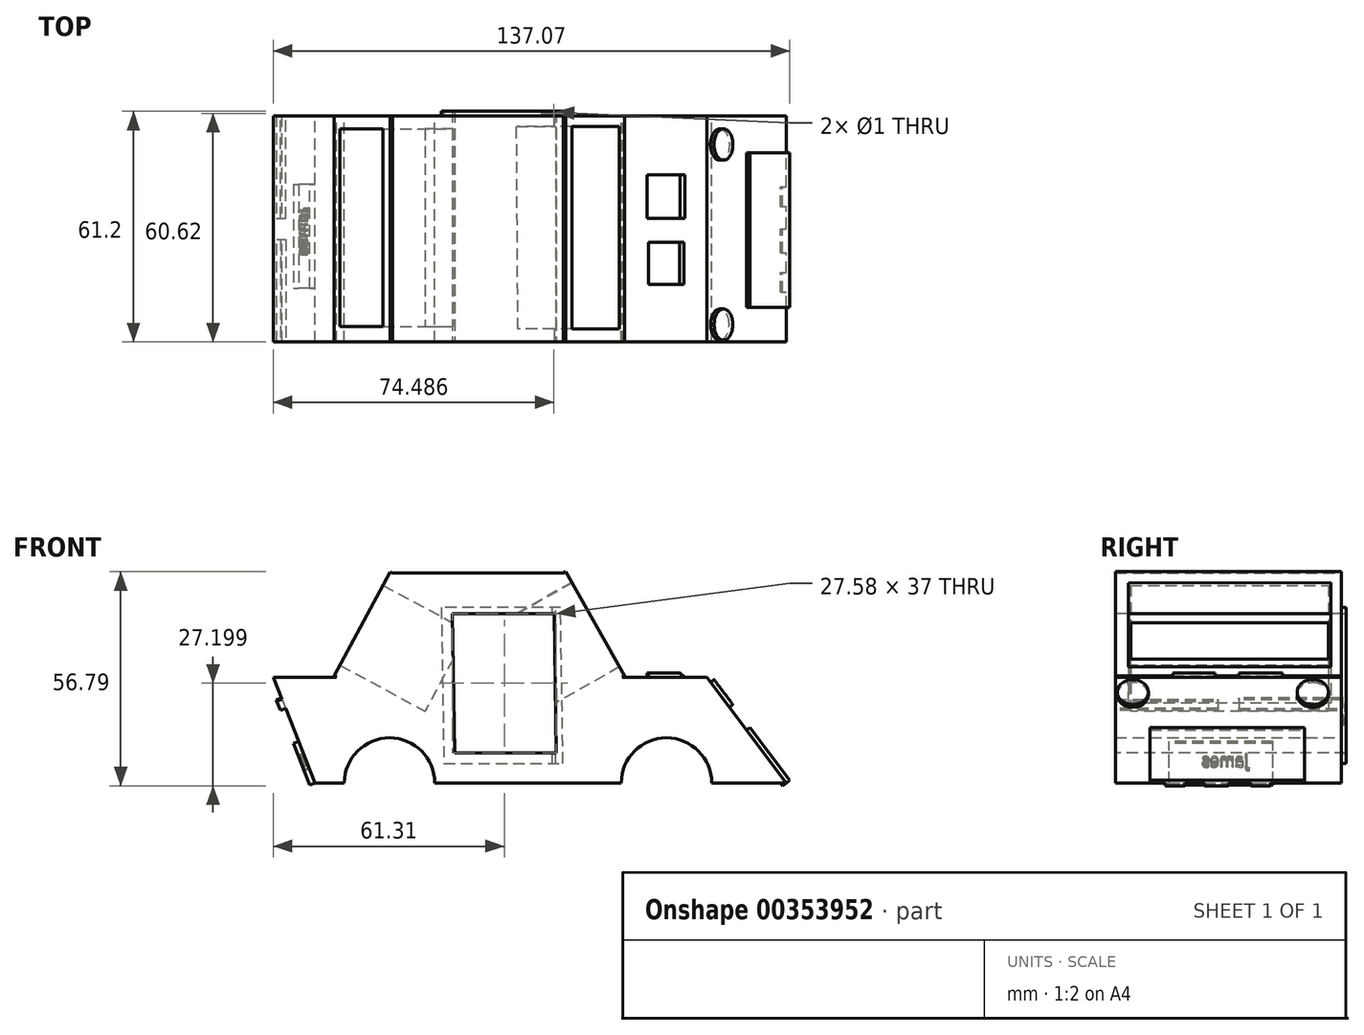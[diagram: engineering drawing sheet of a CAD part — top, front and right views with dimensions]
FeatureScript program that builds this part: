
annotation { "Feature Type Name" : "Feature", "Feature Type Description" : "" }
export const myFeature = defineFeature(function(context is Context, id is Id, definition is map)
    precondition{}
    {
        {
            var Q0;
            Q0=qCreatedBy(makeId("Front.planeOp"),FACE);
            var sketch = newSketch(context, id + "F0", { "sketchPlane" : qUnion([Q0])});
            skLineSegment(sketch, "E0", {"start": v(-59.7, -21.02) * mm, "end": v(-51.97, -21.02) * mm});
            skLineSegment(sketch, "E1", {"start": v(65.31, -21.02) * mm, "end": v(44.23, 7.04) * mm});
            skLineSegment(sketch, "E2", {"start": v(44.23, 7.04) * mm, "end": v(-70.8, 7.04) * mm});
            skLineSegment(sketch, "E3", {"start": v(-70.8, 7.04) * mm, "end": v(-59.7, -21.02) * mm});
            skLineSegment(sketch, "E4", {"start": v(-54.05, 7.04) * mm, "end": v(-39.17, 34.7) * mm});
            skLineSegment(sketch, "E5", {"start": v(-39.17, 34.7) * mm, "end": v(6.2, 34.7) * mm});
            skLineSegment(sketch, "E6", {"start": v(6.2, 34.7) * mm, "end": v(21.82, 7.04) * mm});
            skArc(sketch, "E7", {"start": v(-27.97, -21.02) * mm, "mid": v(-39.97, -9.02) * mm, "end": v(-51.97, -21.02) * mm});
            skArc(sketch, "E8", {"start": v(45.54, -21.02) * mm, "mid": v(33.54, -9.02) * mm, "end": v(21.54, -21.02) * mm});
            skLineSegment(sketch, "E9.trimOffspring", {"start": v(-27.97, -21.02) * mm, "end": v(21.54, -21.02) * mm});
            skLineSegment(sketch, "E10.trimOffspring", {"start": v(45.54, -21.02) * mm, "end": v(65.31, -21.02) * mm});
            skSolve(sketch);
        }
        {
            var Q0;
            {var subQ0=sQuery(id+"F0.wireOp",EDGE,"E4");Q0=makeQuery(id+"F0.imprint","IMPRINT",FACE,{"disambiguationData":[TD([[makeQuery(id+"F0.imprint","IMPRINT",EDGE,{"derivedFrom":subQ0}),-1.0]])]});}
            var Q1;
            Q1=makeQuery(id+"F0.imprint","IMPRINT",FACE,{"disambiguationData":[TD([[makeQuery(id+"F0.imprint","IMPRINT",EDGE,{"derivedFrom":sQuery(id+"F0.wireOp",EDGE,"E0")}),1.0]])]});
            extrude(context, id + "F1", {"entities" : qUnion([Q0, Q1]), "endBound" : BoundingType.SYMMETRIC, "depth" : 60 * mm});
        }
        {
            var Q0;
            Q0=makeQuery(id+"F1.opExtrude","SWEPT_FACE",FACE,{"disambiguationData":[OSD([sQuery(id+"F0.wireOp",EDGE,"E1")])]});
            var sketch = newSketch(context, id + "F2", { "sketchPlane" : qUnion([Q0])});
            skCircle(sketch, "E11", {"center": v(-25.38, -26.75) * mm, "radius": 4.12 * mm});
            skCircle(sketch, "E12", {"center": v(22.39, -26.75) * mm, "radius": 4.16 * mm});
            skLineSegment(sketch, "E13", {"start": v(-20.79, -38.5) * mm, "end": v(-20.79, -56.04) * mm});
            skPoint(sketch, "E13.startSnap0", {"position": v(-30, -38.5) * mm});
            skLineSegment(sketch, "E14", {"start": v(-20.79, -38.5) * mm, "end": v(20.19, -38.5) * mm});
            skLineSegment(sketch, "E15", {"start": v(20.19, -38.5) * mm, "end": v(20.19, -56.04) * mm});
            skLineSegment(sketch, "E16", {"start": v(-16.59, -38.5) * mm, "end": v(-16.59, -56.04) * mm});
            skLineSegment(sketch, "E17", {"start": v(-16.59, -56.04) * mm, "end": v(-11.8, -56.04) * mm});
            skLineSegment(sketch, "E18", {"start": v(-11.8, -56.04) * mm, "end": v(-11.8, -38.5) * mm});
            skLineSegment(sketch, "E19", {"start": v(-11.8, -38.5) * mm, "end": v(-7.8, -38.5) * mm});
            skLineSegment(sketch, "E20", {"start": v(-7.8, -38.5) * mm, "end": v(-7.8, -56.04) * mm});
            skLineSegment(sketch, "E21", {"start": v(-7.8, -56.04) * mm, "end": v(-4.2, -56.04) * mm});
            skLineSegment(sketch, "E22", {"start": v(-4.2, -56.04) * mm, "end": v(-4.2, -38.5) * mm});
            skLineSegment(sketch, "E23", {"start": v(-4.2, -38.5) * mm, "end": v(0, -38.5) * mm});
            skLineSegment(sketch, "E24", {"start": v(0, -38.5) * mm, "end": v(0, -56.04) * mm});
            skLineSegment(sketch, "E25", {"start": v(0, -56.04) * mm, "end": v(4.2, -56.04) * mm});
            skLineSegment(sketch, "E26", {"start": v(4.2, -56.04) * mm, "end": v(4.2, -38.5) * mm});
            skLineSegment(sketch, "E27", {"start": v(4.2, -38.5) * mm, "end": v(8.6, -38.5) * mm});
            skLineSegment(sketch, "E28", {"start": v(8.6, -38.5) * mm, "end": v(8.6, -56.04) * mm});
            skLineSegment(sketch, "E29", {"start": v(8.6, -56.04) * mm, "end": v(12.4, -56.04) * mm});
            skLineSegment(sketch, "E30", {"start": v(12.4, -56.04) * mm, "end": v(12.4, -38.5) * mm});
            skLineSegment(sketch, "E31", {"start": v(12.4, -38.5) * mm, "end": v(15.79, -38.5) * mm});
            skLineSegment(sketch, "E32", {"start": v(15.79, -38.5) * mm, "end": v(15.79, -56.04) * mm});
            skLineSegment(sketch, "E33", {"start": v(15.79, -56.04) * mm, "end": v(20.19, -56.04) * mm});
            skLineSegment(sketch, "E34", {"start": v(20.19, -38.5) * mm, "end": v(-20.79, -38.5) * mm});
            skLineSegment(sketch, "E35", {"start": v(-20.79, -56.04) * mm, "end": v(20.19, -56.04) * mm});
            skLineSegment(sketch, "E36", {"start": v(-30, -34) * mm, "end": v(0, -38.5) * mm});
            skLineSegment(sketch, "E37", {"start": v(0, -38.5) * mm, "end": v(30, -34.5) * mm});
            skSolve(sketch);
        }
        {
            var Q0;
            Q0=makeQuery(id+"F2.imprint","IMPRINT",FACE,{"disambiguationData":[TD([[makeQuery(id+"F2.imprint","IMPRINT",EDGE,{"derivedFrom":sQuery(id+"F2.wireOp",EDGE,"E11")}),1.0]])]});
            var Q1;
            Q1=makeQuery(id+"F2.imprint","IMPRINT",FACE,{"disambiguationData":[TD([[makeQuery(id+"F2.imprint","IMPRINT",EDGE,{"derivedFrom":sQuery(id+"F2.wireOp",EDGE,"E12")}),1.0]])]});
            var Q2;
            {var subQ0=sQuery(id+"F2.wireOp",EDGE,"E13");Q2=makeQuery(id+"F2.imprint","IMPRINT",FACE,{"disambiguationData":[TD([[makeQuery(id+"F2.imprint","IMPRINT",EDGE,{"derivedFrom":subQ0}),1.0]])]});}
            var Q3;
            {var subQ0=sQuery(id+"F2.wireOp",EDGE,"E16");Q3=makeQuery(id+"F2.imprint","IMPRINT",FACE,{"disambiguationData":[TD([[makeQuery(id+"F2.imprint","IMPRINT",EDGE,{"derivedFrom":subQ0}),1.0]])]});}
            var Q4;
            {var subQ0=sQuery(id+"F2.wireOp",EDGE,"E20");Q4=makeQuery(id+"F2.imprint","IMPRINT",FACE,{"disambiguationData":[TD([[makeQuery(id+"F2.imprint","IMPRINT",EDGE,{"derivedFrom":subQ0}),1.0]])]});}
            var Q5;
            {var subQ0=sQuery(id+"F2.wireOp",EDGE,"E18");Q5=makeQuery(id+"F2.imprint","IMPRINT",FACE,{"disambiguationData":[TD([[makeQuery(id+"F2.imprint","IMPRINT",EDGE,{"derivedFrom":subQ0}),-1.0]])]});}
            var Q6;
            {var subQ0=sQuery(id+"F2.wireOp",EDGE,"E22");Q6=makeQuery(id+"F2.imprint","IMPRINT",FACE,{"disambiguationData":[TD([[makeQuery(id+"F2.imprint","IMPRINT",EDGE,{"derivedFrom":subQ0}),-1.0]])]});}
            var Q7;
            {var subQ0=sQuery(id+"F2.wireOp",EDGE,"E24");Q7=makeQuery(id+"F2.imprint","IMPRINT",FACE,{"disambiguationData":[TD([[makeQuery(id+"F2.imprint","IMPRINT",EDGE,{"derivedFrom":subQ0}),1.0]])]});}
            var Q8;
            {var subQ0=sQuery(id+"F2.wireOp",EDGE,"E26");Q8=makeQuery(id+"F2.imprint","IMPRINT",FACE,{"disambiguationData":[TD([[makeQuery(id+"F2.imprint","IMPRINT",EDGE,{"derivedFrom":subQ0}),-1.0]])]});}
            var Q9;
            {var subQ0=sQuery(id+"F2.wireOp",EDGE,"E28");Q9=makeQuery(id+"F2.imprint","IMPRINT",FACE,{"disambiguationData":[TD([[makeQuery(id+"F2.imprint","IMPRINT",EDGE,{"derivedFrom":subQ0}),1.0]])]});}
            var Q10;
            {var subQ0=sQuery(id+"F2.wireOp",EDGE,"E30");Q10=makeQuery(id+"F2.imprint","IMPRINT",FACE,{"disambiguationData":[TD([[makeQuery(id+"F2.imprint","IMPRINT",EDGE,{"derivedFrom":subQ0}),-1.0]])]});}
            var Q11;
            {var subQ0=sQuery(id+"F2.wireOp",EDGE,"E15");Q11=makeQuery(id+"F2.imprint","IMPRINT",FACE,{"disambiguationData":[TD([[makeQuery(id+"F2.imprint","IMPRINT",EDGE,{"derivedFrom":subQ0}),-1.0]])]});}
            extrude(context, id + "F3", {"entities" : qUnion([Q0, Q1, Q2, Q3, Q4, Q5, Q6, Q7, Q8, Q9, Q10, Q11]), "operationType" : NewBodyOperationType.ADD, "depth" : 1.2 * mm});
        }
        {
            var Q0;
            {var subQ0=sQuery(id+"F0.wireOp",EDGE,"E2");Q0=makeQuery(id+"F1.opExtrude","SWEPT_FACE",FACE,{"disambiguationData":[OSD([subQ0]),TDD([makeQuery(id+"F0.imprint","IMPRINT",EDGE,{"disambiguationData":[TD([[makeQuery(id+"F0.imprint","INTERSECT",VERTEX,{"derivedFrom":[sQuery(id+"F0.wireOp",EDGE,"E1"),subQ0]}),-1.0]])],"derivedFrom":subQ0})])]});}
            var sketch = newSketch(context, id + "F4", { "sketchPlane" : qUnion([Q0])});
            skLineSegment(sketch, "E38.bottom", {"start": v(28.38, 14.4) * mm, "end": v(42.17, 14.4) * mm});
            skLineSegment(sketch, "E38.top", {"start": v(28.38, 2.8) * mm, "end": v(42.17, 2.8) * mm});
            skLineSegment(sketch, "E38.left", {"start": v(28.38, 14.4) * mm, "end": v(28.38, 2.8) * mm});
            skLineSegment(sketch, "E38.right", {"start": v(42.17, 14.4) * mm, "end": v(42.17, 2.8) * mm});
            skLineSegment(sketch, "E39.bottom", {"start": v(28.78, -3.6) * mm, "end": v(41.97, -3.6) * mm});
            skLineSegment(sketch, "E39.top", {"start": v(28.78, -14.8) * mm, "end": v(41.97, -14.8) * mm});
            skLineSegment(sketch, "E39.left", {"start": v(28.78, -3.6) * mm, "end": v(28.78, -14.8) * mm});
            skLineSegment(sketch, "E39.right", {"start": v(41.97, -3.6) * mm, "end": v(41.97, -14.8) * mm});
            skSolve(sketch);
        }
        {
            var Q0;
            Q0=makeQuery(id+"F4.imprint","IMPRINT",FACE,{"disambiguationData":[TD([[makeQuery(id+"F4.imprint","IMPRINT",EDGE,{"derivedFrom":sQuery(id+"F4.wireOp",EDGE,"E38.bottom")}),-1.0]])]});
            var Q1;
            Q1=makeQuery(id+"F4.imprint","IMPRINT",FACE,{"disambiguationData":[TD([[makeQuery(id+"F4.imprint","IMPRINT",EDGE,{"derivedFrom":sQuery(id+"F4.wireOp",EDGE,"E39.bottom")}),-1.0]])]});
            extrude(context, id + "F5", {"entities" : qUnion([Q0, Q1]), "operationType" : NewBodyOperationType.ADD, "depth" : 1.2 * mm});
        }
        {
            var Q0;
            Q0=makeQuery(id+"F5.opExtrude","CAP_EDGE",EDGE,{"disambiguationData":[OSD([sQuery(id+"F4.wireOp",EDGE,"E39.right")])],"isStart":false});
            var Q1;
            Q1=makeQuery(id+"F5.opExtrude","CAP_EDGE",EDGE,{"disambiguationData":[OSD([sQuery(id+"F4.wireOp",EDGE,"E38.right")])],"isStart":false});
            chamfer(context, id + "F6", {"entities" : qUnion([Q0, Q1]), "width" : 5 * mm, "tangentPropagation" : true});
        }
        {
            var Q0;
            Q0=makeQuery(id+"F3.opExtrude","CAP_FACE",FACE,{"disambiguationData":[OSD([sQuery(id+"F2.wireOp",EDGE,"E13"),sQuery(id+"F2.wireOp",EDGE,"E15"),sQuery(id+"F2.wireOp",EDGE,"E34"),sQuery(id+"F2.wireOp",EDGE,"E35")])],"isStart":false});
            var sketch = newSketch(context, id + "F7", { "sketchPlane" : qUnion([Q0])});
            skLineSegment(sketch, "E40", {"start": v(-16.79, -38.5) * mm, "end": v(-16.79, -56.04) * mm});
            skLineSegment(sketch, "E41", {"start": v(-11.6, -38.5) * mm, "end": v(-11.6, -56.04) * mm});
            skLineSegment(sketch, "E42", {"start": v(-6.4, -38.5) * mm, "end": v(-6.4, -56.04) * mm});
            skLineSegment(sketch, "E43", {"start": v(-0.3, -38.5) * mm, "end": v(0, -56.04) * mm});
            skLineSegment(sketch, "E44", {"start": v(5.6, -38.5) * mm, "end": v(5.9, -56.04) * mm});
            skLineSegment(sketch, "E45", {"start": v(11.2, -38.5) * mm, "end": v(11.2, -56.04) * mm});
            skLineSegment(sketch, "E46", {"start": v(15.99, -38.5) * mm, "end": v(15.99, -56.04) * mm});
            skSolve(sketch);
        }
        {
            var Q0;
            Q0=makeQuery(id+"F1.opExtrude","SWEPT_FACE",FACE,{"disambiguationData":[OSD([sQuery(id+"F0.wireOp",EDGE,"E6")])]});
            var sketch = newSketch(context, id + "F8", { "sketchPlane" : qUnion([Q0])});
            skLineSegment(sketch, "E47", {"start": v(-26.57, 23.76) * mm, "end": v(-26.57, -1.8) * mm});
            skLineSegment(sketch, "E48", {"start": v(-26.57, -1.8) * mm, "end": v(27.18, -1.8) * mm});
            skLineSegment(sketch, "E49", {"start": v(27.18, -1.8) * mm, "end": v(27.18, 23.93) * mm});
            skLineSegment(sketch, "E50", {"start": v(27.18, 23.93) * mm, "end": v(-26.57, 23.76) * mm});
            skSolve(sketch);
        }
        {
            var Q0;
            Q0=makeQuery(id+"F8.imprint","IMPRINT",FACE,{"disambiguationData":[TD([[makeQuery(id+"F8.imprint","IMPRINT",EDGE,{"derivedFrom":sQuery(id+"F8.wireOp",EDGE,"E47")}),-1.0]])]});
            extrude(context, id + "F9", {"entities" : qUnion([Q0]), "operationType" : NewBodyOperationType.ADD, "depth" : 0.7 * mm});
        }
        {
            var Q0;
            Q0=makeQuery(id+"F1.opExtrude","SWEPT_FACE",FACE,{"disambiguationData":[OSD([sQuery(id+"F0.wireOp",EDGE,"E3")])]});
            var sketch = newSketch(context, id + "F10", { "sketchPlane" : qUnion([Q0])});
            skLineSegment(sketch, "E51", {"start": v(-30, 26.76) * mm, "end": v(-2.8, 26.76) * mm});
            skLineSegment(sketch, "E52", {"start": v(-2.8, 26.76) * mm, "end": v(-2.8, 23.75) * mm});
            skLineSegment(sketch, "E53", {"start": v(-2.8, 23.75) * mm, "end": v(-30, 23.75) * mm});
            skLineSegment(sketch, "E54", {"start": v(30, 26.33) * mm, "end": v(2.8, 26.33) * mm});
            skLineSegment(sketch, "E55", {"start": v(2.8, 26.33) * mm, "end": v(2.8, 23.75) * mm});
            skLineSegment(sketch, "E56", {"start": v(2.8, 23.75) * mm, "end": v(30, 23.75) * mm});
            skLineSegment(sketch, "E57.bottom", {"start": v(-11.8, 2.44) * mm, "end": v(15.79, 2.44) * mm});
            skLineSegment(sketch, "E57.top", {"start": v(-11.8, 14.3) * mm, "end": v(15.79, 14.3) * mm});
            skLineSegment(sketch, "E57.left", {"start": v(-11.8, 2.44) * mm, "end": v(-11.8, 14.3) * mm});
            skLineSegment(sketch, "E57.right", {"start": v(15.79, 2.44) * mm, "end": v(15.79, 14.3) * mm});
            skText(sketch, "E58", { "text": "james", "fontName": "OpenSans-Regular.ttf"});
            const initialGuessF10  = {"E58": [-0.0053, 0.0076, 1, 0, 0.0032]};
            skSetInitialGuess(sketch, initialGuessF10);
            skSolve(sketch);
        }
        {
            var Q0;
            Q0 = qSketchRegion(id + "F10", true);
            var Q1;
            {var subQ0=sQuery(id+"F10.wireOp",EDGE,"E54");Q1=makeQuery(id+"F10.imprint","IMPRINT",FACE,{"disambiguationData":[TD([[makeQuery(id+"F10.imprint","IMPRINT",EDGE,{"derivedFrom":subQ0}),1.0]])]});}
            var Q2;
            {var subQ0=sQuery(id+"F10.wireOp",EDGE,"E51");Q2=makeQuery(id+"F10.imprint","IMPRINT",FACE,{"disambiguationData":[TD([[makeQuery(id+"F10.imprint","IMPRINT",EDGE,{"derivedFrom":subQ0}),-1.0]])]});}
            extrude(context, id + "F11", {"entities" : qUnion([Q0, Q1, Q2]), "operationType" : NewBodyOperationType.ADD, "depth" : 1.5 * mm});
        }
        {
            var Q0;
            Q0=makeQuery(id+"F1.opExtrude","SWEPT_FACE",FACE,{"disambiguationData":[OSD([sQuery(id+"F0.wireOp",EDGE,"E4")])]});
            var sketch = newSketch(context, id + "F12", { "sketchPlane" : qUnion([Q0])});
            skLineSegment(sketch, "E59", {"start": v(-26.5, 7.99) * mm, "end": v(-26.5, -16.16) * mm});
            skLineSegment(sketch, "E60", {"start": v(-26.5, -16.16) * mm, "end": v(25.94, -16.16) * mm});
            skLineSegment(sketch, "E61", {"start": v(25.94, -16.16) * mm, "end": v(25.94, 7.99) * mm});
            skLineSegment(sketch, "E62", {"start": v(25.94, 7.99) * mm, "end": v(-26.5, 7.99) * mm});
            skSolve(sketch);
        }
        {
            var Q0;
            Q0=makeQuery(id+"F12.imprint","IMPRINT",FACE,{"disambiguationData":[TD([[makeQuery(id+"F12.imprint","IMPRINT",EDGE,{"derivedFrom":sQuery(id+"F12.wireOp",EDGE,"E59")}),-1.0]])]});
            extrude(context, id + "F13", {"entities" : qUnion([Q0]), "operationType" : NewBodyOperationType.ADD, "depth" : 0.7 * mm});
        }
        {
            var Q0;
            {var subQ0=sQuery(id+"F0.wireOp",EDGE,"E4");var subQ1=sQuery(id+"F0.wireOp",EDGE,"E3");var subQ2=makeQuery(id+"F1.opExtrude","CAP_EDGE",EDGE,{"disambiguationData":[OSD([subQ1])],"isStart":true});var subQ3=sQuery(id+"F0.wireOp",EDGE,"E6");Q0=makeQuery(id+"F13.boolean.opBoolean","MERGE",FACE,{"derivedFrom":[makeQuery(id+"F11.boolean.opBoolean","MERGE",FACE,{"derivedFrom":[makeQuery(id+"F9.boolean.opBoolean","MERGE",FACE,{"derivedFrom":[makeQuery(id+"F1.opExtrude","CAP_FACE",FACE,{"disambiguationData":[OSD([sQuery(id+"F0.wireOp",EDGE,"E0"),sQuery(id+"F0.wireOp",EDGE,"E1"),sQuery(id+"F0.wireOp",EDGE,"E2"),subQ1,subQ0,sQuery(id+"F0.wireOp",EDGE,"E5"),subQ3,sQuery(id+"F0.wireOp",EDGE,"E7"),sQuery(id+"F0.wireOp",EDGE,"E8"),sQuery(id+"F0.wireOp",EDGE,"E9.trimOffspring"),sQuery(id+"F0.wireOp",EDGE,"E10.trimOffspring")])],"isStart":true}),makeQuery(id+"F9.opExtrude","SWEPT_FACE",FACE,{"disambiguationData":[OSD([subQ3]),TDD([makeQuery(id+"F8.imprint","IMPRINT",EDGE,{"derivedFrom":makeQuery(id+"F1.opExtrude","CAP_EDGE",EDGE,{"disambiguationData":[OSD([subQ3])],"isStart":true})})])]})]}),makeQuery(id+"F11.opExtrude","SWEPT_FACE",FACE,{"disambiguationData":[OSD([subQ1]),TDD([makeQuery(id+"F10.imprint","IMPRINT",EDGE,{"disambiguationData":[TD([[makeQuery(id+"F10.imprint","INTERSECT",VERTEX,{"derivedFrom":[subQ2,sQuery(id+"F10.wireOp",EDGE,"E51")]}),-1.0]])],"derivedFrom":subQ2})])]})]}),makeQuery(id+"F13.opExtrude","SWEPT_FACE",FACE,{"disambiguationData":[OSD([subQ0]),TDD([makeQuery(id+"F12.imprint","IMPRINT",EDGE,{"derivedFrom":makeQuery(id+"F1.opExtrude","CAP_EDGE",EDGE,{"disambiguationData":[OSD([subQ0])],"isStart":true})})])]})]});}
            var sketch = newSketch(context, id + "F14", { "sketchPlane" : qUnion([Q0])});
            skLineSegment(sketch, "E63", {"start": v(-5.43, 25.58) * mm, "end": v(26.2, 25.58) * mm});
            skLineSegment(sketch, "E64", {"start": v(26.2, 25.58) * mm, "end": v(25.55, -15.8) * mm});
            skLineSegment(sketch, "E65", {"start": v(25.55, -15.8) * mm, "end": v(-6.08, -15.8) * mm});
            skLineSegment(sketch, "E66", {"start": v(-6.08, -15.8) * mm, "end": v(-5.43, 25.58) * mm});
            skLineSegment(sketch, "E67", {"start": v(-3.72, 23.96) * mm, "end": v(-4.3, -13.04) * mm});
            skLineSegment(sketch, "E68", {"start": v(-4.3, -13.04) * mm, "end": v(22.7, -13.04) * mm});
            skLineSegment(sketch, "E69", {"start": v(22.7, -13.04) * mm, "end": v(23.28, 23.96) * mm});
            skLineSegment(sketch, "E70", {"start": v(23.28, 23.96) * mm, "end": v(-3.72, 23.96) * mm});
            skSolve(sketch);
        }
        {
            var Q0;
            Q0=makeQuery(id+"F14.imprint","IMPRINT",FACE,{"disambiguationData":[TD([[makeQuery(id+"F14.imprint","IMPRINT",EDGE,{"derivedFrom":sQuery(id+"F14.wireOp",EDGE,"E63")}),-1.0]])]});
            extrude(context, id + "F15", {"entities" : qUnion([Q0]), "operationType" : NewBodyOperationType.ADD, "depth" : 1.2 * mm});
        }
        {
            var Q0;
            Q0=makeQuery(id+"F14.imprint","IMPRINT",FACE,{"disambiguationData":[TD([[makeQuery(id+"F14.imprint","IMPRINT",EDGE,{"derivedFrom":sQuery(id+"F14.wireOp",EDGE,"E67")}),1.0]])]});
            extrude(context, id + "F16", {"entities" : qUnion([Q0]), "operationType" : NewBodyOperationType.REMOVE, "oppositeDirection" : true, "depth" : 66.4 * mm});
        }
        {
            var Q0;
            Q0=makeQuery(id+"F8.imprint","IMPRINT",FACE,{"disambiguationData":[TD([[makeQuery(id+"F8.imprint","IMPRINT",EDGE,{"derivedFrom":sQuery(id+"F8.wireOp",EDGE,"E47")}),1.0]])]});
            extrude(context, id + "F17", {"entities" : qUnion([Q0]), "operationType" : NewBodyOperationType.REMOVE, "oppositeDirection" : true, "depth" : 21.8 * mm});
        }
        {
            var Q0;
            Q0=makeQuery(id+"F12.imprint","IMPRINT",FACE,{"disambiguationData":[TD([[makeQuery(id+"F12.imprint","IMPRINT",EDGE,{"derivedFrom":sQuery(id+"F12.wireOp",EDGE,"E59")}),1.0]])]});
            extrude(context, id + "F18", {"entities" : qUnion([Q0]), "operationType" : NewBodyOperationType.REMOVE, "oppositeDirection" : true, "depth" : 25 * mm});
        }
        {
            var Q0;
            {var subQ0=sQuery(id+"F7.wireOp",EDGE,"E42");Q0=makeQuery(id+"F7.imprint","IMPRINT",FACE,{"disambiguationData":[TD([[makeQuery(id+"F7.imprint","IMPRINT",EDGE,{"derivedFrom":subQ0}),1.0]])]});}
            var Q1;
            {var subQ0=sQuery(id+"F7.wireOp",EDGE,"E44");Q1=makeQuery(id+"F7.imprint","IMPRINT",FACE,{"disambiguationData":[TD([[makeQuery(id+"F7.imprint","IMPRINT",EDGE,{"derivedFrom":subQ0}),1.0]])]});}
            var Q2;
            {var subQ0=sQuery(id+"F7.wireOp",EDGE,"E40");Q2=makeQuery(id+"F7.imprint","IMPRINT",FACE,{"disambiguationData":[TD([[makeQuery(id+"F7.imprint","IMPRINT",EDGE,{"derivedFrom":subQ0}),1.0]])]});}
            extrude(context, id + "F19", {"entities" : qUnion([Q0, Q1, Q2]), "operationType" : NewBodyOperationType.ADD, "oppositeDirection" : true, "depth" : 2.4 * mm});
        }
        {
            var Q0;
            Q0=makeQuery(id+"F15.opExtrude","SWEPT_FACE",FACE,{"disambiguationData":[OSD([sQuery(id+"F14.wireOp",EDGE,"E63")])]});
            var sketch = newSketch(context, id + "F20", { "sketchPlane" : qUnion([Q0])});
            skCircle(sketch, "E71", {"center": v(3.69, 30.62) * mm, "radius": 0.5 * mm});
            skSolve(sketch);
        }
        {
            var Q0;
            Q0=makeQuery(id+"F20.imprint","IMPRINT",FACE,{"disambiguationData":[TD([[makeQuery(id+"F20.imprint","IMPRINT",EDGE,{"derivedFrom":sQuery(id+"F20.wireOp",EDGE,"E71")}),1.0]])]});
            extrude(context, id + "F21", {"entities" : qUnion([Q0]), "operationType" : NewBodyOperationType.REMOVE, "oppositeDirection" : true, "depth" : 45.5 * mm});
        }
    });
